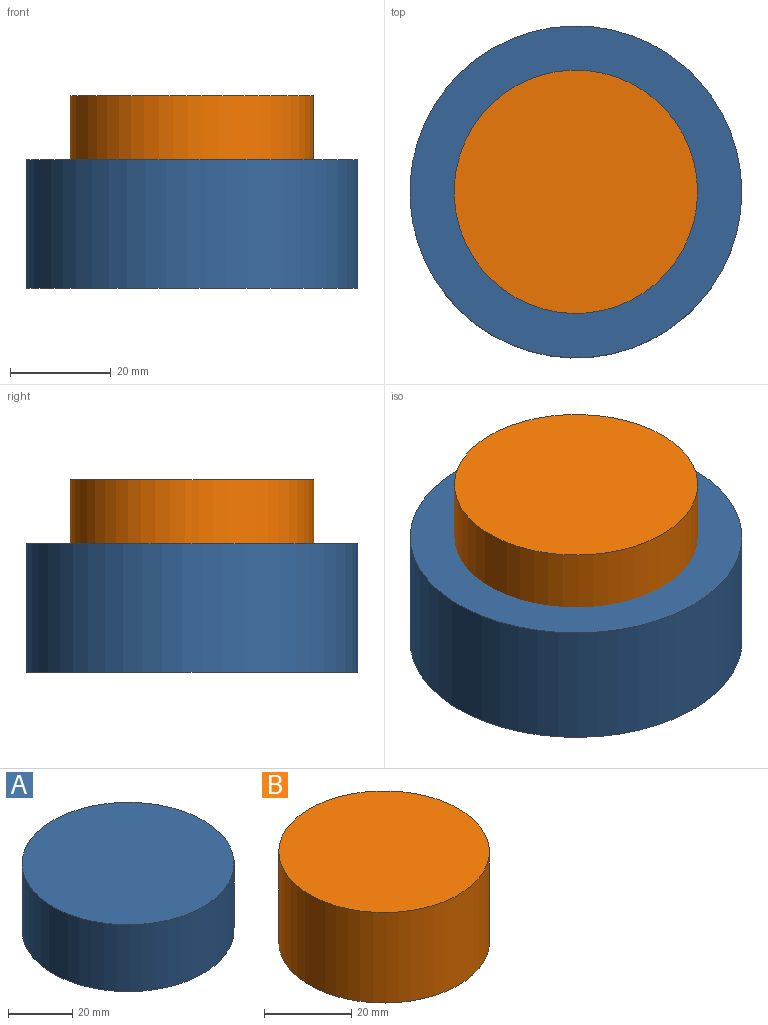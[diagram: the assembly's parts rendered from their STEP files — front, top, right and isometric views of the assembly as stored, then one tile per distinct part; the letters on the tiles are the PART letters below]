
ASSEMBLY  parts=2 mates=1
PART A: 3 faces, bbox 65.9x65.9x25.4 mm
  f0: cylinder r=32.93mm len=65.85mm, axis (0,0,-1), area 5254.7mm2, adj f1,f2
  f1: plane 65.85x65.85mm, normal (0,0,1), area 3405.8mm2, adj f0
  f2: plane 65.85x65.85mm, normal (0,0,-1), area 3405.8mm2, adj f0
PART B: 3 faces, bbox 48.3x48.3x25.4 mm
  f0: cylinder r=24.14mm len=48.28mm, axis (0,0,-1), area 3852.7mm2, adj f1,f2
  f1: plane 48.28x48.28mm, normal (0,0,1), area 1830.8mm2, adj f0
  f2: plane 48.28x48.28mm, normal (0,0,-1), area 1830.8mm2, adj f0
PLACE A t=(6.48,61.66,-35.51)mm
PLACE B t=(-1.03,1.13,2.59)mm
MATE fastened A.f0 <-> B.f0  axis (0,0,1) through (-49.33,44,15.29)mm
